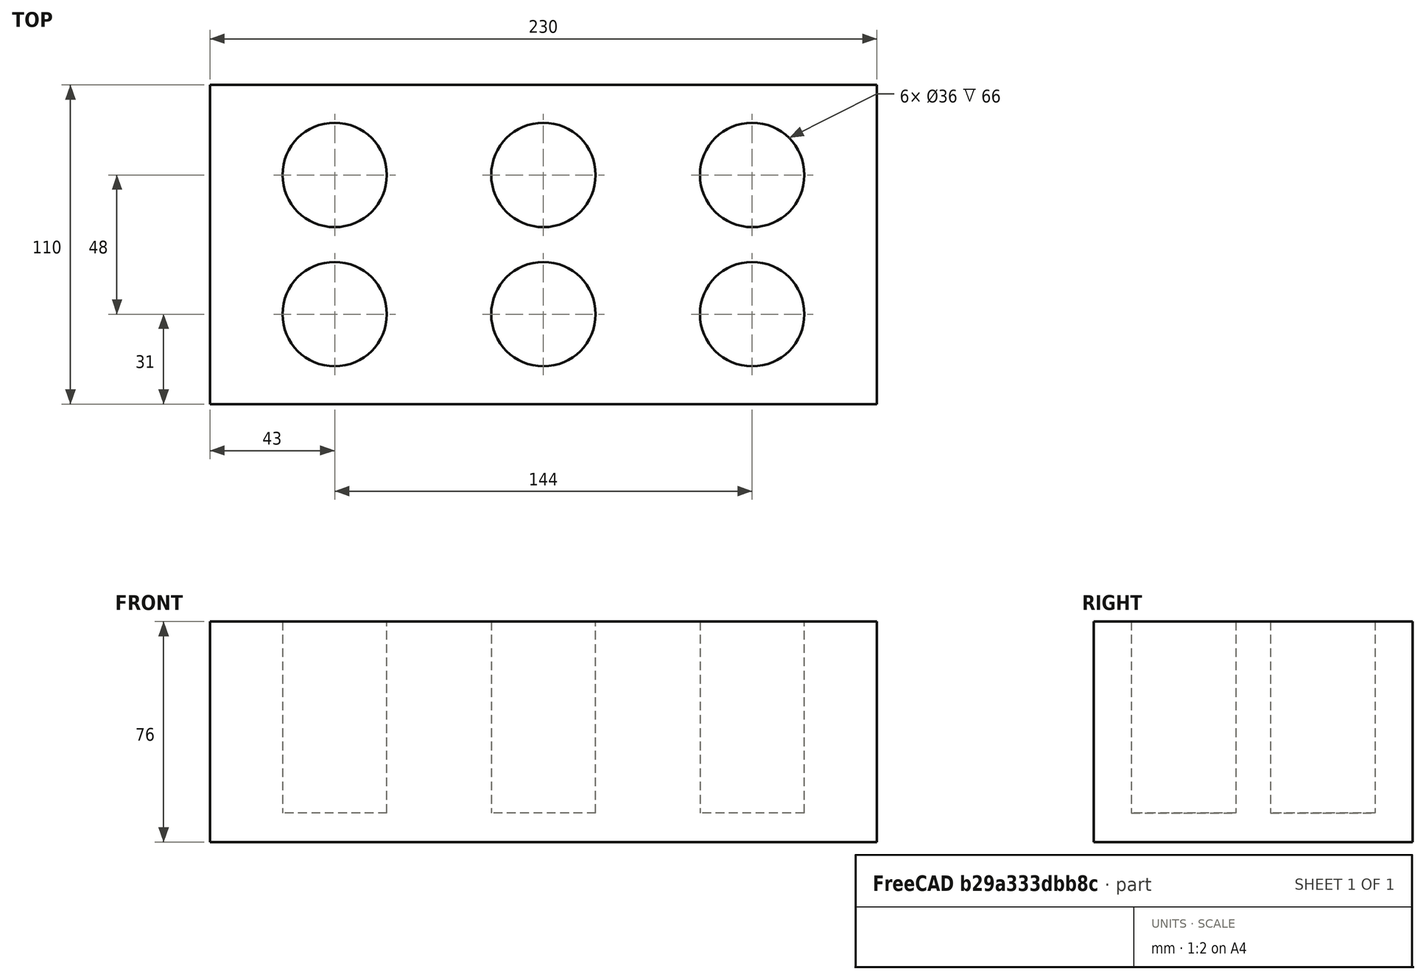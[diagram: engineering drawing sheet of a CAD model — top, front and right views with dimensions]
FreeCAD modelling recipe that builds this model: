
FCSTD DOCUMENT  (FreeCAD 1.0R39319 (Git))
Label: ojt1_t09r02_brick
License: All rights reserved
LicenseURL: https://en.wikipedia.org/wiki/All_rights_reserved
objects: Part::Cylinder×6, Part::MultiFuse×4, PartDesign::Body×1, Part::Box×1, Part::Cut×1
note: 13 computed .brp shape members not serialized (recipe doc carries the construction recipe); baked Part::Feature solids carry a one-line shape summary decoded from their .brp

FEATURE [PartDesign::Body] Body  label="Cos"
  AllowCompound = false
  Origin = -> Origin
FEATURE [Part::Box] Box  label="base"
  AttacherType = Attacher::AttachEngine3D
  Height = 76
  Length = 230
  Width = 110
FEATURE [Part::Cylinder] Cylinder  label="cilindre 001"
  Angle = 360
  AttacherType = Attacher::AttachEngine3D
  FirstAngle = 0
  Height = 80
  Placement = pos=(43,31,0) rot=(0,0,1;0rad)
  Radius = 18
  SecondAngle = 0
FEATURE [Part::Cylinder] Cylinder001  label="cilindre 002"
  Angle = 360
  AttacherType = Attacher::AttachEngine3D
  FirstAngle = 0
  Height = 80
  Placement = pos=(43,79,0) rot=(0,0,1;0rad)
  Radius = 18
  SecondAngle = 0
FEATURE [Part::MultiFuse] Fusion
  Shapes = -> [Cylinder,Cylinder001]
FEATURE [Part::Cylinder] Cylinder002  label="cilindre 003"
  Angle = 360
  AttacherType = Attacher::AttachEngine3D
  FirstAngle = 0
  Height = 80
  Placement = pos=(43,31,0) rot=(0,0,1;0rad)
  Radius = 18
  SecondAngle = 0
FEATURE [Part::Cylinder] Cylinder003  label="cilindre 004"
  Angle = 360
  AttacherType = Attacher::AttachEngine3D
  FirstAngle = 0
  Height = 80
  Placement = pos=(43,79,0) rot=(0,0,1;0rad)
  Radius = 18
  SecondAngle = 0
FEATURE [Part::MultiFuse] Fusion001
  Placement = pos=(72,0,0) rot=(0,0,1;0rad)
  Shapes = -> [Cylinder002,Cylinder003]
FEATURE [Part::Cylinder] Cylinder004  label="cilindre 005"
  Angle = 360
  AttacherType = Attacher::AttachEngine3D
  FirstAngle = 0
  Height = 80
  Placement = pos=(43,31,0) rot=(0,0,1;0rad)
  Radius = 18
  SecondAngle = 0
FEATURE [Part::Cylinder] Cylinder005  label="cilindre 006"
  Angle = 360
  AttacherType = Attacher::AttachEngine3D
  FirstAngle = 0
  Height = 80
  Placement = pos=(43,79,0) rot=(0,0,1;0rad)
  Radius = 18
  SecondAngle = 0
FEATURE [Part::MultiFuse] Fusion002
  Placement = pos=(144,0,0) rot=(0,0,1;0rad)
  Shapes = -> [Cylinder004,Cylinder005]
FEATURE [Part::MultiFuse] Fusion003
  Placement = pos=(0,0,10) rot=(0,0,1;0rad)
  Shapes = -> [Fusion,Fusion001,Fusion002]
FEATURE [Part::Cut] Cut
  Base = -> Box
  Tool = -> Fusion003
